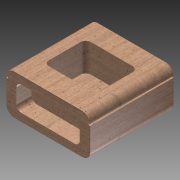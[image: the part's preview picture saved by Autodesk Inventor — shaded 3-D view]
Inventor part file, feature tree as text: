
AUTODESK INVENTOR PART (.ipt)
format: ipt  version: 2015 (Build 190159000, 159)  size: 218,624 bytes
history: native  units: in
note: dims shown in document units (in); Inventor stores cm internally (conversion verified against a paired STEP export)
features: extrude x4, sketch x4, fillet x2
ambient origin geometry x8: Origin, YZ Plane, XZ Plane, XY Plane, X Axis, Y Axis, Z Axis, Center Point
bodies: Solid1 (feature_tree)
feature tree (10):
  extrude  "Extrusion1"  Depth=1.53in
  extrude  "Extrusion2"  Depth=2.4in
  extrude  "Extrusion3"  Depth=0.57in TaperAngle=0.0deg
  extrude  "Extrusion4"  Depth=2.5in
  fillet  "Fillet1"  Radius=1.0in
  fillet  "Fillet2"  Radius=0.57in
  sketch  "Sketch1"  dims[d0=3.17in d1=1.53in]
  sketch  "Sketch2"  dims[d2=3.17in d3=0.0in d4=2.4in]
  sketch  "Sketch3"  dims[d5=0.93in d7=0.57in d8=0.0in]
  sketch  "Sketch4"  dims[d9=0.2in d10=2.5in d11=1.0in d12=0.57in d13=0.0in d14=0.3in d15=0.82in d16=1.59in d17=1.975in d18=1.07in d19=0.0in d20=0.06in d21=0.3in d23=0.01in]
